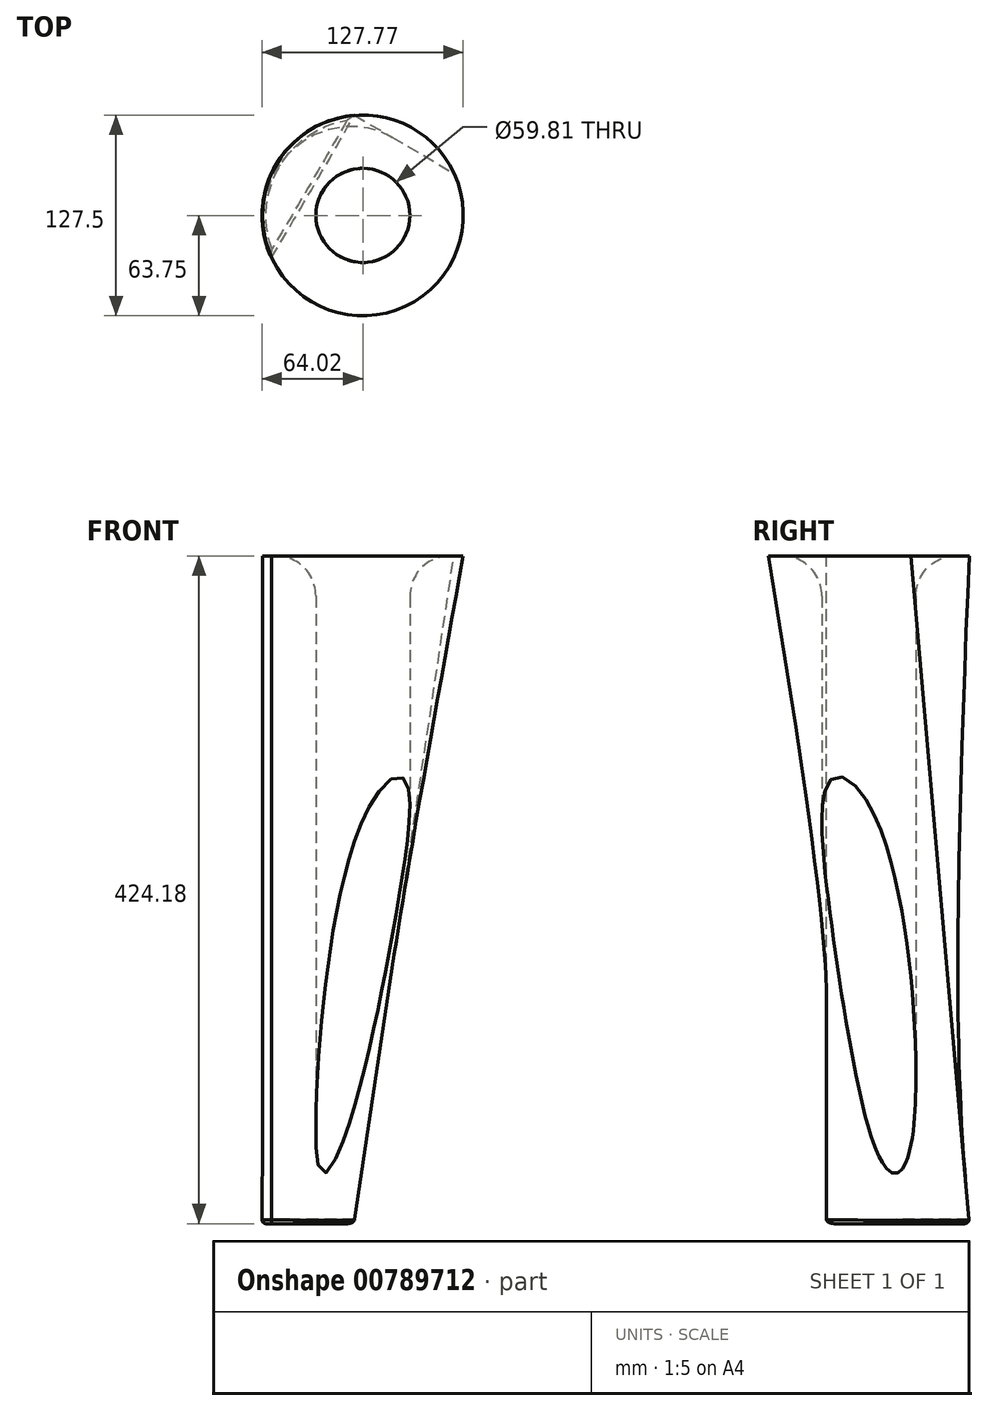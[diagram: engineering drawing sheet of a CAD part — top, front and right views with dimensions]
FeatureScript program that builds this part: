
annotation { "Feature Type Name" : "Feature", "Feature Type Description" : "" }
export const myFeature = defineFeature(function(context is Context, id is Id, definition is map)
    precondition{}
    {
        {
            var Q0;
            Q0=qCreatedBy(makeId("Top.planeOp"),FACE);
            var sketch = newSketch(context, id + "F0", { "sketchPlane" : qUnion([Q0])});
            skPoint(sketch, "E0.0.midPoint", {"position": v(23.62, -40.84) * mm});
            skCircle(sketch, "E1", {"center": v(0, 0) * mm, "radius": 64.04 * mm});
            skCircle(sketch, "E2.cCircle", {"center": v(0, 0) * mm, "radius": 36.84 * mm, "construction": true});
            skLineSegment(sketch, "E2.0", {"start": v(63.8, -36.84) * mm, "end": v(-63.8, -36.84) * mm});
            skLineSegment(sketch, "E2.1", {"start": v(-63.8, -36.84) * mm, "end": v(0, 73.67) * mm});
            skLineSegment(sketch, "E2.2", {"start": v(0, 73.67) * mm, "end": v(63.8, -36.84) * mm});
            skPoint(sketch, "E2.0.midPoint", {"position": v(0, -36.84) * mm});
            skSolve(sketch);
        }
        {
            var Q0;
            Q0=qCreatedBy(makeId("Top.planeOp"),FACE);
            cPlane(context, id + "F1", {"entities" : qUnion([Q0]), "cplaneType" : CPlaneType.OFFSET, "offset" : 424.18 * mm, "width" : 152.4 * mm, "height" : 152.4 * mm});
        }
        {
            var Q0;
            Q0=qCreatedBy(id+"F1.planeOp",FACE);
            var sketch = newSketch(context, id + "F2", { "sketchPlane" : qUnion([Q0])});
            skCircle(sketch, "E3", {"center": v(0, 0) * mm, "radius": 63.75 * mm});
            skSolve(sketch);
        }
        {
            var Q0;
            {var subQ1=sQuery(id+"F0.wireOp",EDGE,"E1");var subQ6=sQuery(id+"F0.wireOp",EDGE,"E2.1");var subQ9=makeQuery(id+"F0.imprint","INTERSECT",VERTEX,{"disambiguationData":[OD(0.0)],"derivedFrom":[subQ1,subQ6]});Q0=makeQuery(id+"F0.imprint","IMPRINT",FACE,{"disambiguationData":[TD([[makeQuery(id+"F0.imprint","IMPRINT",EDGE,{"disambiguationData":[TD([[subQ9,1.0]])],"derivedFrom":subQ1}),1.0]])]});}
            var Q1;
            Q1=makeQuery(id+"F2.imprint","IMPRINT",FACE,{"disambiguationData":[TD([[makeQuery(id+"F2.imprint","IMPRINT",EDGE,{"derivedFrom":sQuery(id+"F2.wireOp",EDGE,"E3")}),1.0]])]});
            loft(context, id + "F3", {"sheetProfilesArray" : [{ "sheetProfileEntities" : qUnion([Q0]) }, { "sheetProfileEntities" : qUnion([Q1]) }]});
        }
        {
            var Q0;
            {var subQ1=sQuery(id+"F0.wireOp",EDGE,"E1");var subQ6=sQuery(id+"F0.wireOp",EDGE,"E2.1");var subQ9=makeQuery(id+"F0.imprint","INTERSECT",VERTEX,{"disambiguationData":[OD(0.0)],"derivedFrom":[subQ1,subQ6]});Q0=makeQuery(id+"F3.opLoft","CAP_FACE",FACE,{"disambiguationData":[OSD([makeQuery(id+"F0.imprint","IMPRINT",FACE,{"disambiguationData":[TD([[makeQuery(id+"F0.imprint","IMPRINT",EDGE,{"disambiguationData":[TD([[subQ9,1.0]])],"derivedFrom":subQ1}),1.0]])]})])],"isStart":true});}
            var sketch = newSketch(context, id + "F4", { "sketchPlane" : qUnion([Q0])});
            skCircle(sketch, "E4", {"center": v(0, 0) * mm, "radius": 29.9 * mm});
            skSolve(sketch);
        }
        {
            var Q0;
            Q0 = qSketchRegion(id + "F4", true);
            extrude(context, id + "F5", {"entities" : qUnion([Q0]), "operationType" : NewBodyOperationType.REMOVE, "oppositeDirection" : true, "depth" : 464.82 * mm, "offsetDistance" : 25.4 * mm});
        }
        {
            var Q0;
            Q0=makeQuery(id+"F5.boolean.opBoolean","INTERSECT",EDGE,{"derivedFrom":[makeQuery(id+"F3.opLoft","CAP_FACE",FACE,{"disambiguationData":[OSD([makeQuery(id+"F2.imprint","IMPRINT",FACE,{"disambiguationData":[TD([[makeQuery(id+"F2.imprint","IMPRINT",EDGE,{"derivedFrom":sQuery(id+"F2.wireOp",EDGE,"E3")}),1.0]])]})])],"isStart":true}),makeQuery(id+"F5.opExtrude","SWEPT_FACE",FACE,{"disambiguationData":[OSD([sQuery(id+"F4.wireOp",EDGE,"E4")])]})]});
            fillet(context, id + "F6", {"entities" : qUnion([Q0]), "radius" : 25.4 * mm, "tangentPropagation" : true, "allowEdgeOverflow" : false});
        }
        {
            var Q0;
            Q0=makeQuery(id+"F5.boolean.opBoolean","COPY",EDGE,{"derivedFrom":makeQuery(id+"F5.opExtrude","CAP_EDGE",EDGE,{"disambiguationData":[OSD([sQuery(id+"F4.wireOp",EDGE,"E4")])],"isStart":true})});
            var Q1;
            {var subQ1=sQuery(id+"F0.wireOp",EDGE,"E1");var subQ6=sQuery(id+"F0.wireOp",EDGE,"E2.1");var subQ9=makeQuery(id+"F0.imprint","INTERSECT",VERTEX,{"disambiguationData":[OD(0.0)],"derivedFrom":[subQ1,subQ6]});Q1=makeQuery(id+"F3.opLoft","CAP_FACE",FACE,{"disambiguationData":[OSD([makeQuery(id+"F0.imprint","IMPRINT",FACE,{"disambiguationData":[TD([[makeQuery(id+"F0.imprint","IMPRINT",EDGE,{"disambiguationData":[TD([[subQ9,1.0]])],"derivedFrom":subQ1}),1.0]])]})])],"isStart":true});}
            fillet(context, id + "F7", {"entities" : qUnion([Q0, Q1]), "radius" : 2.54 * mm, "tangentPropagation" : true, "allowEdgeOverflow" : false});
        }
    });
